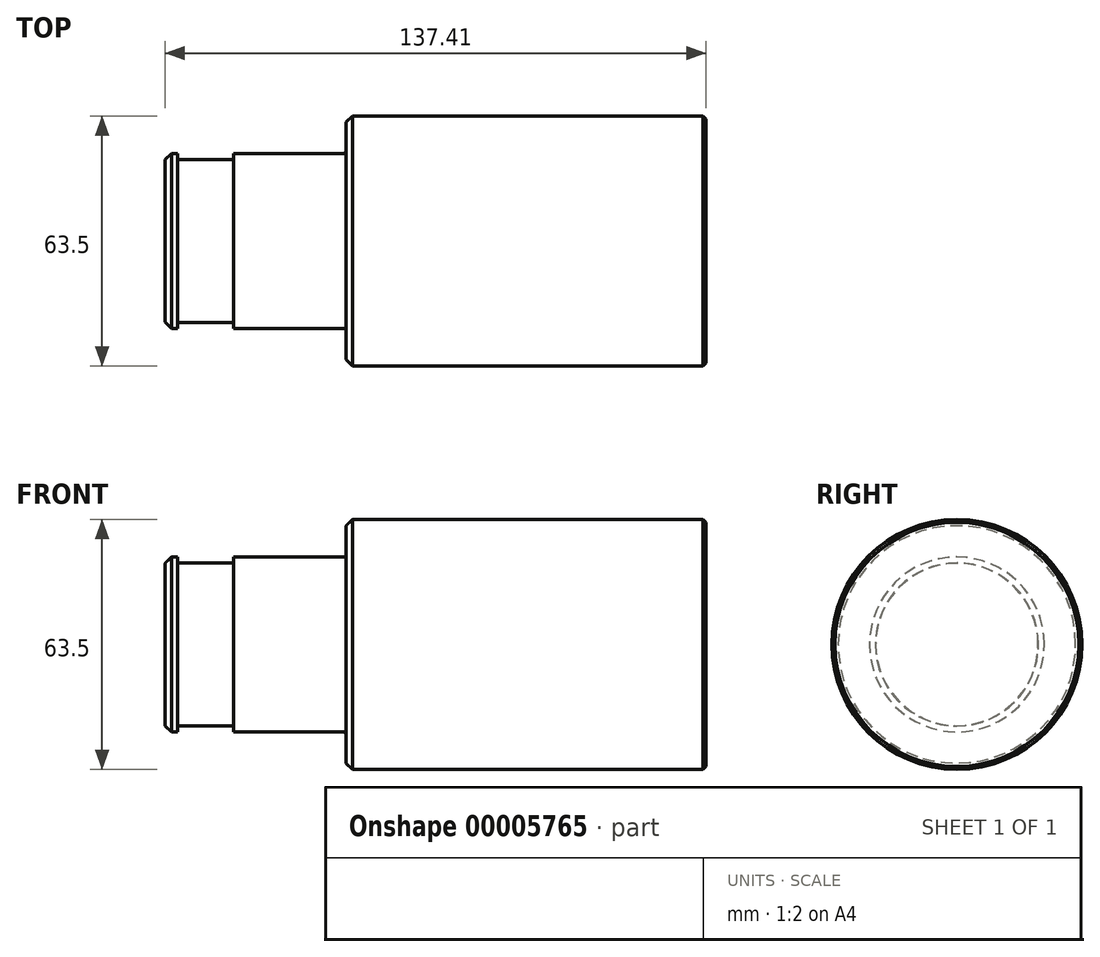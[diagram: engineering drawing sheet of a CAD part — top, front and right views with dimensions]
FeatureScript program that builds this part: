
annotation { "Feature Type Name" : "Feature", "Feature Type Description" : "" }
export const myFeature = defineFeature(function(context is Context, id is Id, definition is map)
    precondition{}
    {
        {
            var Q0;
            Q0=qCreatedBy(makeId("Front.planeOp"),FACE);
            var sketch = newSketch(context, id + "F0", { "sketchPlane" : qUnion([Q0])});
            skLineSegment(sketch, "E0", {"start": v(-137.41, 0) * mm, "end": v(0, 0) * mm});
            skLineSegment(sketch, "E1.0", {"start": v(-91.44, -31.75) * mm, "end": v(0, -31.75) * mm});
            skLineSegment(sketch, "E2", {"start": v(0, 0) * mm, "end": v(0, -31.75) * mm});
            skLineSegment(sketch, "E3.0", {"start": v(-91.44, -22.23) * mm, "end": v(-91.44, -31.75) * mm});
            skLineSegment(sketch, "E4.0", {"start": v(-137.41, -22.23) * mm, "end": v(-134.24, -22.23) * mm});
            skLineSegment(sketch, "E5.0", {"start": v(-137.41, 0) * mm, "end": v(-137.41, -22.23) * mm});
            skLineSegment(sketch, "E6.0", {"start": v(-134.24, -20.7) * mm, "end": v(-134.24, -22.23) * mm});
            skLineSegment(sketch, "E7.0", {"start": v(-120.02, -20.7) * mm, "end": v(-120.02, -22.23) * mm});
            skLineSegment(sketch, "E8.0", {"start": v(-134.24, -20.7) * mm, "end": v(-120.02, -20.7) * mm});
            skLineSegment(sketch, "E9.trimOffspring", {"start": v(-120.01, -22.23) * mm, "end": v(-91.44, -22.23) * mm});
            skPoint(sketch, "E10.orphan", {"position": v(-127.87, 0) * mm});
            skSolve(sketch);
        }
        {
            var Q0;
            Q0=makeQuery(id+"F0.imprint","IMPRINT",FACE,{"disambiguationData":[TD([[makeQuery(id+"F0.imprint","IMPRINT",EDGE,{"derivedFrom":sQuery(id+"F0.wireOp",EDGE,"E0")}),-1.0]])]});
            var Q1;
            Q1=sQuery(id+"F0.wireOp",EDGE,"E0");
            revolve(context, id + "F1", {"entities" : qUnion([Q0]), "axis" : qUnion([Q1]), "revolveType" : RevolveType.FULL});
        }
        {
            var Q0;
            Q0=makeQuery(id+"F1.opRevolve","SWEPT_EDGE",EDGE,{"disambiguationData":[OSD([sQuery(id+"F0.wireOp",EDGE,"E4.0"),sQuery(id+"F0.wireOp",EDGE,"E5.0")])]});
            chamfer(context, id + "F2", {"entities" : qUnion([Q0]), "width" : 1.59 * mm, "tangentPropagation" : true});
        }
        {
            var Q0;
            Q0=makeQuery(id+"F1.opRevolve","SWEPT_EDGE",EDGE,{"disambiguationData":[OSD([sQuery(id+"F0.wireOp",EDGE,"E1.0"),sQuery(id+"F0.wireOp",EDGE,"E3.0")])]});
            chamfer(context, id + "F3", {"entities" : qUnion([Q0]), "width" : 1.59 * mm, "tangentPropagation" : true});
        }
        {
            var Q0;
            Q0=makeQuery(id+"F1.opRevolve","SWEPT_EDGE",EDGE,{"disambiguationData":[OSD([sQuery(id+"F0.wireOp",EDGE,"E3.0"),sQuery(id+"F0.wireOp",EDGE,"E9.trimOffspring")])]});
            fillet(context, id + "F4", {"entities" : qUnion([Q0]), "radius" : 0.76 * mm, "tangentPropagation" : true, "allowEdgeOverflow" : false});
        }
        {
            var Q0;
            Q0=makeQuery(id+"F1.opRevolve","SWEPT_EDGE",EDGE,{"disambiguationData":[OSD([sQuery(id+"F0.wireOp",EDGE,"E1.0"),sQuery(id+"F0.wireOp",EDGE,"E2")])]});
            chamfer(context, id + "F5", {"entities" : qUnion([Q0]), "width" : 0.76 * mm, "tangentPropagation" : true});
        }
    });
